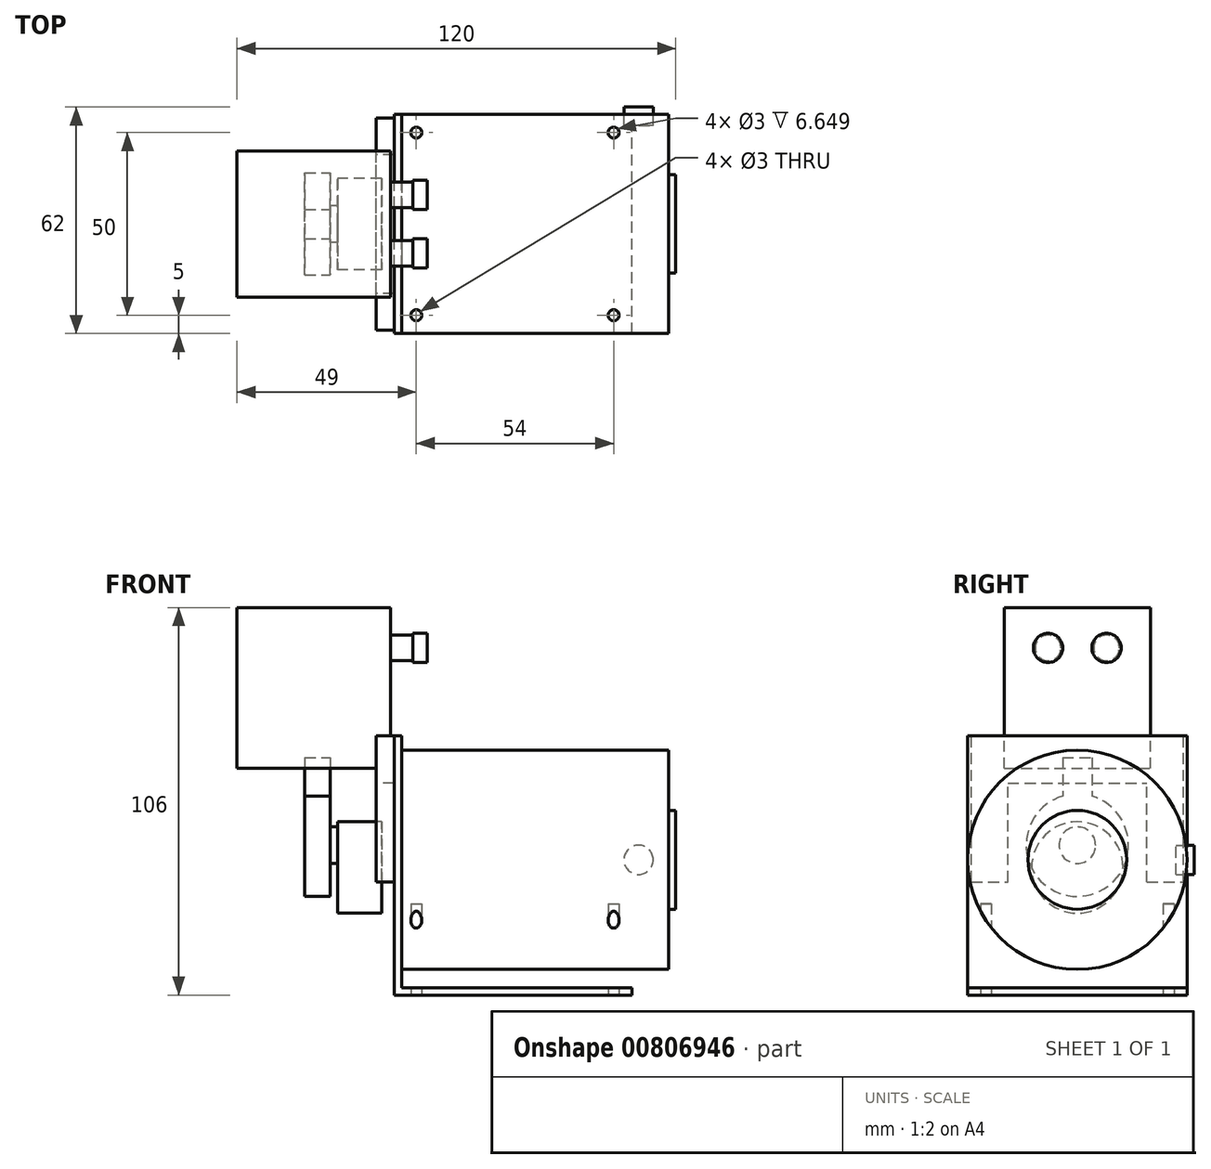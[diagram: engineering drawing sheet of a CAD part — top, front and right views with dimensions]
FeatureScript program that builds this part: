
annotation { "Feature Type Name" : "Feature", "Feature Type Description" : "" }
export const myFeature = defineFeature(function(context is Context, id is Id, definition is map)
    precondition{}
    {
        {
            var Q0;
            Q0=qCreatedBy(makeId("Top.planeOp"),FACE);
            var sketch = newSketch(context, id + "F0", { "sketchPlane" : qUnion([Q0])});
            skLineSegment(sketch, "E0.bottom", {"start": v(32.5, -30) * mm, "end": v(-32.5, -30) * mm});
            skLineSegment(sketch, "E0.top", {"start": v(32.5, 30) * mm, "end": v(-32.5, 30) * mm});
            skLineSegment(sketch, "E0.left", {"start": v(32.5, -30) * mm, "end": v(32.5, 30) * mm});
            skLineSegment(sketch, "E0.right", {"start": v(-32.5, -30) * mm, "end": v(-32.5, 30) * mm});
            skPoint(sketch, "E0.middle", {"position": v(0, 0) * mm});
            skCircle(sketch, "E1", {"center": v(22.5, -20) * mm, "radius": 2.2 * mm, "construction": true});
            skCircle(sketch, "E2.0.1.0", {"center": v(22.5, 20) * mm, "radius": 2.2 * mm, "construction": true});
            skCircle(sketch, "E2.1.0.0", {"center": v(-32.5, -20) * mm, "radius": 2.2 * mm, "construction": true});
            skCircle(sketch, "E2.1.1.0", {"center": v(-32.5, 20) * mm, "radius": 2.2 * mm, "construction": true});
            skLineSegment(sketch, "E2.direction1", {"start": v(22.5, -20) * mm, "end": v(-32.5, -20) * mm, "construction": true});
            skLineSegment(sketch, "E2.direction2", {"start": v(22.5, -20) * mm, "end": v(22.5, 20) * mm, "construction": true});
            skSolve(sketch);
        }
        {
            var Q0;
            Q0=makeQuery(id+"F0.imprint","IMPRINT",FACE,{"disambiguationData":[TD([[makeQuery(id+"F0.imprint","IMPRINT",EDGE,{"derivedFrom":sQuery(id+"F0.wireOp",EDGE,"E0.bottom")}),-1.0]])]});
            extrude(context, id + "F1", {"entities" : qUnion([Q0]), "depth" : 2 * mm, "offsetDistance" : 25 * mm});
        }
        {
            var Q0;
            Q0=makeQuery(id+"F1.opExtrude","CAP_FACE",FACE,{"disambiguationData":[OSD([sQuery(id+"F0.wireOp",EDGE,"E0.bottom"),sQuery(id+"F0.wireOp",EDGE,"E0.top"),sQuery(id+"F0.wireOp",EDGE,"E0.left"),sQuery(id+"F0.wireOp",EDGE,"E0.right")])],"isStart":false});
            var sketch = newSketch(context, id + "F2", { "sketchPlane" : qUnion([Q0])});
            skLineSegment(sketch, "E3.bottom", {"start": v(-32.5, 30) * mm, "end": v(-30.5, 30) * mm});
            skLineSegment(sketch, "E3.top", {"start": v(-32.5, -30) * mm, "end": v(-30.5, -30) * mm});
            skLineSegment(sketch, "E3.left", {"start": v(-32.5, 30) * mm, "end": v(-32.5, -30) * mm});
            skLineSegment(sketch, "E3.right", {"start": v(-30.5, 30) * mm, "end": v(-30.5, -30) * mm});
            skSolve(sketch);
        }
        {
            var Q0;
            Q0=makeQuery(id+"F2.imprint","IMPRINT",FACE,{"disambiguationData":[TD([[makeQuery(id+"F2.imprint","IMPRINT",EDGE,{"derivedFrom":sQuery(id+"F2.wireOp",EDGE,"E3.bottom")}),1.0]])]});
            extrude(context, id + "F3", {"entities" : qUnion([Q0]), "operationType" : NewBodyOperationType.ADD, "depth" : (71 - 2) * mm, "offsetDistance" : 25 * mm});
        }
        {
            var Q0;
            Q0=makeQuery(id+"F3.opExtrude","SWEPT_FACE",FACE,{"disambiguationData":[OSD([sQuery(id+"F2.wireOp",EDGE,"E3.right")])]});
            var sketch = newSketch(context, id + "F4", { "sketchPlane" : qUnion([Q0])});
            skCircle(sketch, "E4", {"center": v(0, 37) * mm, "radius": 30 * mm});
            skSolve(sketch);
        }
        {
            var Q0;
            {var subQ0=sQuery(id+"F4.wireOp",EDGE,"E4");var subQ1=sQuery(id+"F2.wireOp",EDGE,"E3.right");var subQ2=makeQuery(id+"F4.imprint","INTERSECT",VERTEX,{"derivedFrom":[makeQuery(id+"F3.opExtrude","SWEPT_EDGE",EDGE,{"disambiguationData":[OSD([sQuery(id+"F0.wireOp",EDGE,"E0.top"),sQuery(id+"F2.wireOp",EDGE,"E3.bottom"),subQ1])]}),subQ0]});Q0=makeQuery(id+"F4.imprint","IMPRINT",FACE,{"disambiguationData":[TD([[makeQuery(id+"F4.imprint","IMPRINT",EDGE,{"disambiguationData":[TD([[subQ2,-1.0]])],"derivedFrom":subQ0}),1.0]])]});}
            extrude(context, id + "F5", {"entities" : qUnion([Q0]), "depth" : 73 * mm, "offsetDistance" : 25 * mm});
        }
        {
            var Q0;
            Q0=makeQuery(id+"F5.opExtrude","CAP_FACE",FACE,{"disambiguationData":[OSD([sQuery(id+"F4.wireOp",EDGE,"E4")])],"isStart":false});
            var sketch = newSketch(context, id + "F6", { "sketchPlane" : qUnion([Q0])});
            skCircle(sketch, "E5", {"center": v(0, 37) * mm, "radius": 13.5 * mm});
            skSolve(sketch);
        }
        {
            var Q0;
            Q0=makeQuery(id+"F6.imprint","IMPRINT",FACE,{"disambiguationData":[TD([[makeQuery(id+"F6.imprint","IMPRINT",EDGE,{"derivedFrom":sQuery(id+"F6.wireOp",EDGE,"E5")}),1.0]])]});
            extrude(context, id + "F7", {"entities" : qUnion([Q0]), "operationType" : NewBodyOperationType.ADD, "depth" : 2 * mm, "offsetDistance" : 25 * mm});
        }
        {
            var Q0;
            Q0=makeQuery(id+"F3.boolean.opBoolean","MERGE",FACE,{"derivedFrom":[makeQuery(id+"F1.opExtrude","SWEPT_FACE",FACE,{"disambiguationData":[OSD([sQuery(id+"F0.wireOp",EDGE,"E0.right")])]}),makeQuery(id+"F3.opExtrude","SWEPT_FACE",FACE,{"disambiguationData":[OSD([sQuery(id+"F2.wireOp",EDGE,"E3.left")])]})]});
            var sketch = newSketch(context, id + "F8", { "sketchPlane" : qUnion([Q0])});
            skLineSegment(sketch, "E6.bottom", {"start": v(29, 31) * mm, "end": v(-29, 31) * mm});
            skLineSegment(sketch, "E6.top", {"start": v(29, 71) * mm, "end": v(-29, 71) * mm});
            skLineSegment(sketch, "E6.left", {"start": v(29, 31) * mm, "end": v(29, 71) * mm});
            skLineSegment(sketch, "E6.right", {"start": v(-29, 31) * mm, "end": v(-29, 71) * mm});
            skPoint(sketch, "E6.middle", {"position": v(0, 51) * mm});
            skSolve(sketch);
        }
        {
            var Q0;
            Q0 = qSketchRegion(id + "F8", true);
            extrude(context, id + "F9", {"entities" : qUnion([Q0]), "depth" : 5 * mm, "offsetDistance" : 25 * mm});
        }
        {
            var Q0;
            Q0=makeQuery(id+"F9.opExtrude","CAP_FACE",FACE,{"disambiguationData":[OSD([sQuery(id+"F8.wireOp",EDGE,"E6.bottom"),sQuery(id+"F8.wireOp",EDGE,"E6.top"),sQuery(id+"F8.wireOp",EDGE,"E6.left"),sQuery(id+"F8.wireOp",EDGE,"E6.right")])],"isStart":false});
            var sketch = newSketch(context, id + "F10", { "sketchPlane" : qUnion([Q0])});
            skLineSegment(sketch, "E7.bottom", {"start": v(19, 31) * mm, "end": v(-19, 31) * mm});
            skLineSegment(sketch, "E7.top", {"start": v(19, 58) * mm, "end": v(-19, 58) * mm});
            skLineSegment(sketch, "E7.left", {"start": v(19, 31) * mm, "end": v(19, 58) * mm});
            skLineSegment(sketch, "E7.right", {"start": v(-19, 31) * mm, "end": v(-19, 58) * mm});
            skPoint(sketch, "E7.middle", {"position": v(0, 44.5) * mm});
            skSolve(sketch);
        }
        {
            var Q0;
            Q0 = qSketchRegion(id + "F10", true);
            extrude(context, id + "F11", {"entities" : qUnion([Q0]), "operationType" : NewBodyOperationType.REMOVE, "endBound" : BoundingType.UP_TO_NEXT, "oppositeDirection" : true, "depth" : 25 * mm, "offsetDistance" : 25 * mm});
        }
        {
            var Q0;
            Q0=makeQuery(id+"F9.opExtrude","CAP_FACE",FACE,{"disambiguationData":[OSD([sQuery(id+"F8.wireOp",EDGE,"E6.bottom"),sQuery(id+"F8.wireOp",EDGE,"E6.top"),sQuery(id+"F8.wireOp",EDGE,"E6.left"),sQuery(id+"F8.wireOp",EDGE,"E6.right")])],"isStart":false});
            var sketch = newSketch(context, id + "F12", { "sketchPlane" : qUnion([Q0])});
            skLineSegment(sketch, "E8.bottom", {"start": v(20, 62) * mm, "end": v(-20, 62) * mm});
            skLineSegment(sketch, "E8.top", {"start": v(20, 106) * mm, "end": v(-20, 106) * mm});
            skLineSegment(sketch, "E8.left", {"start": v(20, 62) * mm, "end": v(20, 106) * mm});
            skLineSegment(sketch, "E8.right", {"start": v(-20, 62) * mm, "end": v(-20, 106) * mm});
            skPoint(sketch, "E8.middle", {"position": v(0, 84) * mm});
            skSolve(sketch);
        }
        {
            var Q0;
            Q0 = qSketchRegion(id + "F12", true);
            extrude(context, id + "F13", {"entities" : qUnion([Q0]), "operationType" : NewBodyOperationType.ADD, "depth" : 38 * mm, "offsetDistance" : 25 * mm});
        }
        {
            var Q0;
            Q0=makeQuery(id+"F13.opExtrude","CAP_FACE",FACE,{"disambiguationData":[OSD([sQuery(id+"F12.wireOp",EDGE,"E8.bottom"),sQuery(id+"F12.wireOp",EDGE,"E8.top"),sQuery(id+"F12.wireOp",EDGE,"E8.left"),sQuery(id+"F12.wireOp",EDGE,"E8.right")])],"isStart":true});
            var sketch = newSketch(context, id + "F14", { "sketchPlane" : qUnion([Q0])});
            skSolve(sketch);
        }
        {
            var Q0;
            Q0 = qSketchRegion(id + "F14", true);
            var Q1;
            {var subQ0=sQuery(id+"F12.wireOp",EDGE,"E8.top");Q1=makeQuery(id+"F14.imprint","IMPRINT",FACE,{"disambiguationData":[TD([[makeQuery(id+"F14.imprint","IMPRINT",EDGE,{"derivedFrom":makeQuery(id+"F13.opExtrude","CAP_EDGE",EDGE,{"disambiguationData":[OSD([subQ0])],"isStart":true})}),-1.0]])]});}
            extrude(context, id + "F15", {"entities" : qUnion([Q0, Q1]), "operationType" : NewBodyOperationType.ADD, "depth" : 4 * mm, "offsetDistance" : 25 * mm});
        }
        {
            var Q0;
            Q0=makeQuery(id+"F15.opExtrude","CAP_FACE",FACE,{"disambiguationData":[OSD([sQuery(id+"F8.wireOp",EDGE,"E6.top"),sQuery(id+"F12.wireOp",EDGE,"E8.top"),sQuery(id+"F12.wireOp",EDGE,"E8.left"),sQuery(id+"F12.wireOp",EDGE,"E8.right")])],"isStart":false});
            var sketch = newSketch(context, id + "F16", { "sketchPlane" : qUnion([Q0])});
            skCircle(sketch, "E9", {"center": v(8, 95) * mm, "radius": 3.5 * mm});
            skLineSegment(sketch, "E10", {"start": v(0, 106) * mm, "end": v(0, 80) * mm, "construction": true});
            skCircle(sketch, "E11.MirrorC", {"center": v(-8, 95) * mm, "radius": 3.5 * mm});
            skSolve(sketch);
        }
        {
            var Q0;
            Q0 = qSketchRegion(id + "F16", true);
            extrude(context, id + "F17", {"entities" : qUnion([Q0]), "operationType" : NewBodyOperationType.ADD, "depth" : 6 * mm, "offsetDistance" : 25 * mm});
        }
        {
            var Q0;
            Q0=makeQuery(id+"F17.opExtrude","CAP_FACE",FACE,{"disambiguationData":[OSD([sQuery(id+"F16.wireOp",EDGE,"E9")])],"isStart":false});
            var sketch = newSketch(context, id + "F18", { "sketchPlane" : qUnion([Q0])});
            skCircle(sketch, "E12", {"center": v(8, 95) * mm, "radius": 4 * mm});
            skLineSegment(sketch, "E13", {"start": v(0, 105.2) * mm, "end": v(0, 80.31) * mm, "construction": true});
            skCircle(sketch, "E14.MirrorC", {"center": v(-8, 95) * mm, "radius": 4 * mm});
            skSolve(sketch);
        }
        {
            var Q0;
            Q0 = qSketchRegion(id + "F18", true);
            extrude(context, id + "F19", {"entities" : qUnion([Q0]), "operationType" : NewBodyOperationType.ADD, "depth" : 4 * mm, "offsetDistance" : 25 * mm});
        }
        {
            var Q0;
            Q0=makeQuery(id+"F9.opExtrude","CAP_FACE",FACE,{"disambiguationData":[OSD([sQuery(id+"F8.wireOp",EDGE,"E6.bottom"),sQuery(id+"F8.wireOp",EDGE,"E6.top"),sQuery(id+"F8.wireOp",EDGE,"E6.left"),sQuery(id+"F8.wireOp",EDGE,"E6.right")])],"isStart":false});
            cPlane(context, id + "F20", {"entities" : qUnion([Q0]), "cplaneType" : CPlaneType.OFFSET, "offset" : 16 * mm, "width" : 150 * mm, "height" : 150 * mm});
        }
        {
            var Q0;
            Q0=qCreatedBy(id+"F20.planeOp",FACE);
            var sketch = newSketch(context, id + "F21", { "sketchPlane" : qUnion([Q0])});
            skCircle(sketch, "E15", {"center": v(0, 41) * mm, "radius": 14 * mm});
            skCircle(sketch, "E16.0", {"center": v(0, 37) * mm, "radius": 30 * mm});
            skLineSegment(sketch, "E17.bottom", {"start": v(4, 65) * mm, "end": v(-4, 65) * mm});
            skLineSegment(sketch, "E17.top", {"start": v(4, 43.02) * mm, "end": v(-4, 43.02) * mm});
            skLineSegment(sketch, "E17.left", {"start": v(4, 65) * mm, "end": v(4, 43.02) * mm});
            skLineSegment(sketch, "E17.right", {"start": v(-4, 65) * mm, "end": v(-4, 43.02) * mm});
            skPoint(sketch, "E17.middle", {"position": v(0, 54.01) * mm});
            skSolve(sketch);
        }
        {
            var Q0;
            Q0=makeQuery(id+"F21.imprint","IMPRINT",FACE,{"disambiguationData":[TD([[makeQuery(id+"F21.imprint","IMPRINT",EDGE,{"derivedFrom":sQuery(id+"F21.wireOp",EDGE,"E15")}),1.0]])]});
            var Q1;
            {var subQ5=sQuery(id+"F21.wireOp",EDGE,"E17.bottom");Q1=makeQuery(id+"F21.imprint","IMPRINT",FACE,{"disambiguationData":[TD([[makeQuery(id+"F21.imprint","IMPRINT",EDGE,{"derivedFrom":subQ5}),1.0]])]});}
            extrude(context, id + "F22", {"entities" : qUnion([Q0, Q1]), "endBound" : BoundingType.SYMMETRIC, "depth" : 7 * mm, "offsetDistance" : 25 * mm});
        }
        {
            var Q0;
            Q0=makeQuery(id+"F22.opExtrude","CAP_FACE",FACE,{"disambiguationData":[OSD([sQuery(id+"F21.wireOp",EDGE,"E15"),sQuery(id+"F21.wireOp",EDGE,"E17.bottom"),sQuery(id+"F21.wireOp",EDGE,"E17.left"),sQuery(id+"F21.wireOp",EDGE,"E17.right")])],"isStart":true});
            var sketch = newSketch(context, id + "F23", { "sketchPlane" : qUnion([Q0])});
            skCircle(sketch, "E18", {"center": v(0, 41) * mm, "radius": 5 * mm});
            skSolve(sketch);
        }
        {
            var Q0;
            Q0 = qSketchRegion(id + "F23", true);
            extrude(context, id + "F24", {"entities" : qUnion([Q0]), "operationType" : NewBodyOperationType.ADD, "depth" : 2 * mm, "offsetDistance" : 25 * mm});
        }
        {
            var Q0;
            Q0=makeQuery(id+"F24.opExtrude","CAP_FACE",FACE,{"disambiguationData":[OSD([sQuery(id+"F23.wireOp",EDGE,"E18")])],"isStart":false});
            var sketch = newSketch(context, id + "F25", { "sketchPlane" : qUnion([Q0])});
            skCircle(sketch, "E19", {"center": v(0, 34.9) * mm, "radius": 12.5 * mm});
            skSolve(sketch);
        }
        {
            var Q0;
            Q0 = qSketchRegion(id + "F25", true);
            extrude(context, id + "F26", {"entities" : qUnion([Q0]), "operationType" : NewBodyOperationType.ADD, "depth" : 12 * mm, "offsetDistance" : 25 * mm});
        }
        {
            var Q0;
            Q0=qCreatedBy(makeId("Front.planeOp"),FACE);
            cPlane(context, id + "F27", {"entities" : qUnion([Q0]), "cplaneType" : CPlaneType.OFFSET, "offset" : 32 * mm, "oppositeDirection" : true, "width" : 150 * mm, "height" : 150 * mm});
        }
        {
            var Q0;
            Q0=qCreatedBy(id+"F27.planeOp",FACE);
            var sketch = newSketch(context, id + "F28", { "sketchPlane" : qUnion([Q0])});
            skLineSegment(sketch, "E20", {"start": v(-30.5, 67) * mm, "end": v(42.5, 67) * mm});
            skLineSegment(sketch, "E21", {"start": v(42.5, 7) * mm, "end": v(-30.5, 7) * mm});
            skLineSegment(sketch, "E22", {"start": v(42.5, 67) * mm, "end": v(42.5, 7) * mm});
            skCircle(sketch, "E23", {"center": v(34.33, 37) * mm, "radius": 4 * mm});
            skPoint(sketch, "E23.centerSnap0", {"position": v(42.5, 37) * mm});
            skSolve(sketch);
        }
        {
            var Q0;
            Q0 = qSketchRegion(id + "F28", true);
            extrude(context, id + "F29", {"entities" : qUnion([Q0]), "depth" : 5 * mm, "offsetDistance" : 25 * mm});
        }
        {
            var Q0;
            Q0=makeQuery(id+"F1.opExtrude","CAP_FACE",FACE,{"disambiguationData":[OSD([sQuery(id+"F0.wireOp",EDGE,"E0.bottom"),sQuery(id+"F0.wireOp",EDGE,"E0.top"),sQuery(id+"F0.wireOp",EDGE,"E0.left"),sQuery(id+"F0.wireOp",EDGE,"E0.right")])],"isStart":true});
            var sketch = newSketch(context, id + "F30", { "sketchPlane" : qUnion([Q0])});
            skCircle(sketch, "E24", {"center": v(27.5, 25) * mm, "radius": 1.5 * mm});
            skCircle(sketch, "E25.0.1.0", {"center": v(27.5, -25) * mm, "radius": 1.5 * mm});
            skCircle(sketch, "E25.1.0.0", {"center": v(-26.5, 25) * mm, "radius": 1.5 * mm});
            skCircle(sketch, "E25.1.1.0", {"center": v(-26.5, -25) * mm, "radius": 1.5 * mm});
            skLineSegment(sketch, "E25.direction1", {"start": v(27.5, 25) * mm, "end": v(-26.5, 25) * mm, "construction": true});
            skLineSegment(sketch, "E25.direction2", {"start": v(27.5, 25) * mm, "end": v(27.5, -25) * mm, "construction": true});
            skSolve(sketch);
        }
        {
            var Q0;
            Q0 = qSketchRegion(id + "F30", true);
            extrude(context, id + "F31", {"entities" : qUnion([Q0]), "operationType" : NewBodyOperationType.REMOVE, "oppositeDirection" : true, "depth" : 25 * mm, "offsetDistance" : 25 * mm});
        }
    });
